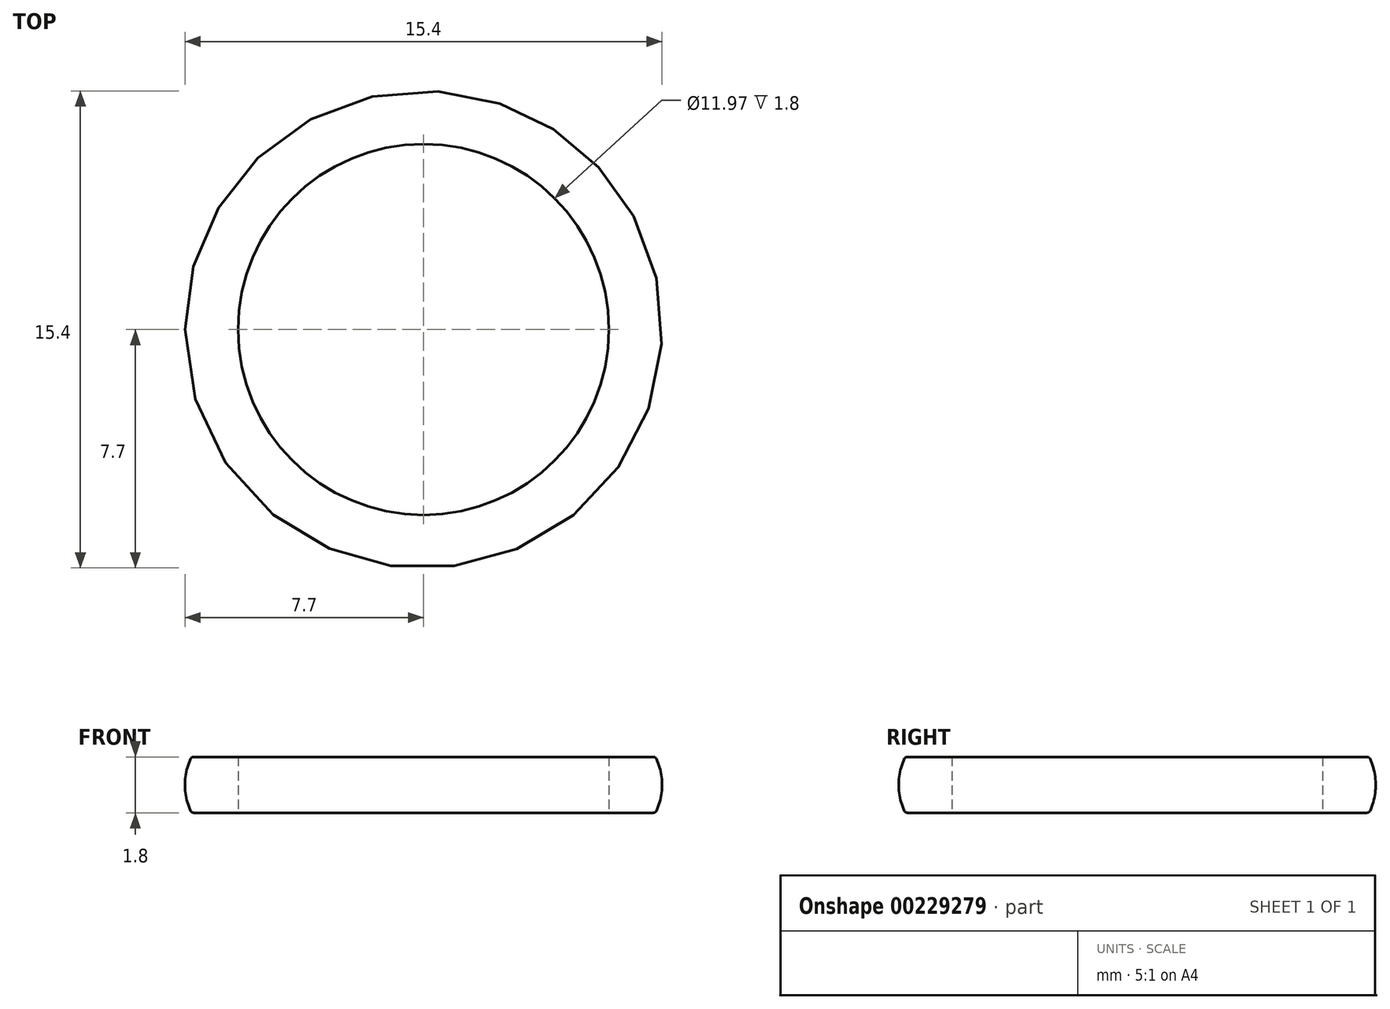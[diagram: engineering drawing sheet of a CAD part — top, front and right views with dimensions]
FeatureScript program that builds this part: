
annotation { "Feature Type Name" : "Feature", "Feature Type Description" : "" }
export const myFeature = defineFeature(function(context is Context, id is Id, definition is map)
    precondition{}
    {
        {
            var Q0;
            Q0=qCreatedBy(makeId("Front.planeOp"),FACE);
            var sketch = newSketch(context, id + "F0", { "sketchPlane" : qUnion([Q0])});
            skLineSegment(sketch, "E0.bottom", {"start": v(-7.49, 0.9) * mm, "end": v(-5.99, 0.9) * mm});
            skLineSegment(sketch, "E0.top", {"start": v(-7.49, -0.9) * mm, "end": v(-5.99, -0.9) * mm});
            skLineSegment(sketch, "E0.left", {"start": v(-7.49, 0.9) * mm, "end": v(-7.49, -0.9) * mm});
            skLineSegment(sketch, "E0.right", {"start": v(-5.99, 0.9) * mm, "end": v(-5.99, -0.9) * mm});
            skPoint(sketch, "E0.middle", {"position": v(-6.74, 0) * mm});
            skLineSegment(sketch, "E1", {"start": v(0, 0) * mm, "end": v(0, 9.63) * mm});
            skCircle(sketch, "E2", {"center": v(-5.7, 0) * mm, "radius": 2 * mm});
            skSolve(sketch);
        }
        {
            var Q0;
            Q0=makeQuery(id+"F0.imprint","IMPRINT",FACE,{"disambiguationData":[TD([[makeQuery(id+"F0.imprint","IMPRINT",EDGE,{"derivedFrom":sQuery(id+"F0.wireOp",EDGE,"E0.bottom")}),-1.0]])]});
            var Q1;
            {var subQ0=sQuery(id+"F0.wireOp",EDGE,"E0.left");Q1=makeQuery(id+"F0.imprint","IMPRINT",FACE,{"disambiguationData":[TD([[makeQuery(id+"F0.imprint","IMPRINT",EDGE,{"derivedFrom":subQ0}),-1.0]])]});}
            var Q2;
            Q2=sQuery(id+"F0.wireOp",EDGE,"E1");
            revolve(context, id + "F1", {"entities" : qUnion([Q0, Q1]), "axis" : qUnion([Q2]), "revolveType" : RevolveType.FULL});
        }
        {
            var Q0;
            Q0=makeQuery(id+"F1.opRevolve","SWEPT_EDGE",EDGE,{"disambiguationData":[OSD([sQuery(id+"F0.wireOp",EDGE,"E0.bottom"),sQuery(id+"F0.wireOp",EDGE,"E0.left"),sQuery(id+"F0.wireOp",EDGE,"E2")])]});
            var Q1;
            Q1=makeQuery(id+"F1.opRevolve","SWEPT_EDGE",EDGE,{"disambiguationData":[OSD([sQuery(id+"F0.wireOp",EDGE,"E0.top"),sQuery(id+"F0.wireOp",EDGE,"E0.left"),sQuery(id+"F0.wireOp",EDGE,"E2")])]});
            fillet(context, id + "F2", {"entities" : qUnion([Q0, Q1]), "radius" : 0.1 * mm, "tangentPropagation" : true, "allowEdgeOverflow" : false});
        }
    });
